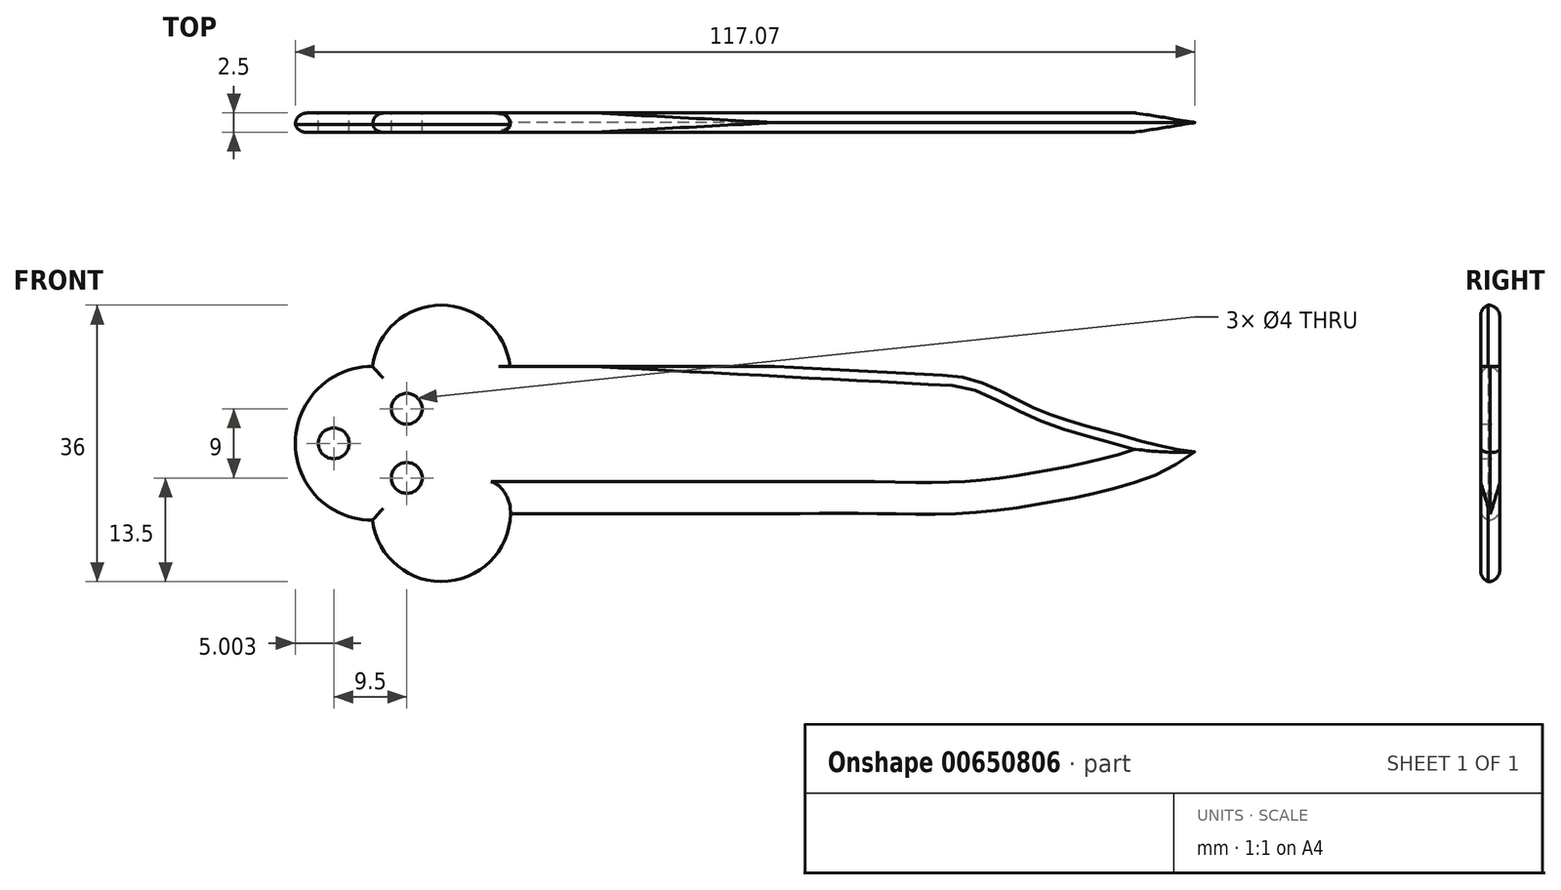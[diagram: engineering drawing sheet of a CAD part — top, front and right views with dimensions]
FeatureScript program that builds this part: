
annotation { "Feature Type Name" : "Feature", "Feature Type Description" : "" }
export const myFeature = defineFeature(function(context is Context, id is Id, definition is map)
    precondition{}
    {
        {
            var Q0;
            Q0=qCreatedBy(makeId("Front.planeOp"),FACE);
            var sketch = newSketch(context, id + "F0", { "sketchPlane" : qUnion([Q0])});
            skLineSegment(sketch, "E0", {"start": v(-50.99, 0) * mm, "end": v(69.01, 0) * mm});
            skPoint(sketch, "E1", {"position": v(-40.99, 0) * mm});
            skPoint(sketch, "E2", {"position": v(-31.99, 0) * mm});
            skCircle(sketch, "E3", {"center": v(-40.99, 0) * mm, "radius": 10 * mm});
            skLineSegment(sketch, "E4", {"start": v(-31.99, 9) * mm, "end": v(-31.99, 0) * mm});
            skLineSegment(sketch, "E5", {"start": v(-31.99, -9) * mm, "end": v(-31.99, 0) * mm});
            skCircle(sketch, "E6", {"center": v(-31.99, 9) * mm, "radius": 9 * mm});
            skCircle(sketch, "E7", {"center": v(-31.99, -9) * mm, "radius": 9 * mm});
            skLineSegment(sketch, "E8", {"start": v(-40.99, 0) * mm, "end": v(-31.99, 9) * mm});
            skLineSegment(sketch, "E9", {"start": v(-40.99, 0) * mm, "end": v(-31.99, -9) * mm});
            skPoint(sketch, "E10", {"position": v(-36.49, 4.5) * mm});
            skPoint(sketch, "E11", {"position": v(-36.49, -4.5) * mm});
            skLineSegment(sketch, "E12", {"start": v(-50.99, 0) * mm, "end": v(-40.99, 0) * mm});
            skLineSegment(sketch, "E13", {"start": v(-50.99, 0) * mm, "end": v(-45.99, 0) * mm});
            skPoint(sketch, "E14", {"position": v(-45.99, 0) * mm});
            skCircle(sketch, "E15", {"center": v(-45.99, 0) * mm, "radius": 2 * mm});
            skCircle(sketch, "E16", {"center": v(-36.49, 4.5) * mm, "radius": 2 * mm});
            skCircle(sketch, "E17", {"center": v(-36.49, -4.5) * mm, "radius": 2 * mm});
            skPoint(sketch, "E18", {"position": v(-40.93, -10) * mm});
            skLineSegment(sketch, "E19", {"start": v(-40.93, -10) * mm, "end": v(-23.04, -10) * mm});
            skPoint(sketch, "E20", {"position": v(-40.93, 10) * mm});
            skLineSegment(sketch, "E21", {"start": v(-40.93, 10) * mm, "end": v(-23.04, 10) * mm});
            skLineSegment(sketch, "E22", {"start": v(-23.04, 10) * mm, "end": v(-23.04, -10) * mm});
            skLineSegment(sketch, "E23", {"start": v(-23.04, 10) * mm, "end": v(34.9, 10) * mm});
            skFitSpline(sketch, "E24", {"points": [v(34.9, 10) * mm, v(45.52, 5.83) * mm, v(55.56, 2.58) * mm, v(69.01, 0) * mm], "startDerivative": vector(32.43, -1.73) * mm, "endDerivative": vector(41.87, 0) * mm});
            skLineSegment(sketch, "E25", {"start": v(-23.04, -10) * mm, "end": v(7.16, -10) * mm});
            skFitSpline(sketch, "E26", {"points": [v(7.16, -10) * mm, v(14.98, -10) * mm, v(24.87, -10) * mm, v(35.5, -10) * mm, v(46.7, -8.63) * mm, v(61.16, -4.94) * mm, v(69.01, 0) * mm], "startDerivative": vector(52.92, -0.1) * mm, "endDerivative": vector(44.23, 34.13) * mm});
            skSolve(sketch);
        }
        {
            var Q0;
            Q0 = qSketchRegion(id + "F0", true);
            var Q1;
            {var subQ0=sQuery(id+"F0.wireOp",EDGE,"E23");Q1=makeQuery(id+"F0.imprint","IMPRINT",FACE,{"disambiguationData":[TD([[makeQuery(id+"F0.imprint","IMPRINT",EDGE,{"derivedFrom":subQ0}),-1.0]])]});}
            var Q2;
            {var subQ0=sQuery(id+"F0.wireOp",EDGE,"E4");var subQ1=sQuery(id+"F0.wireOp",EDGE,"E3");var subQ2=makeQuery(id+"F0.imprint","INTERSECT",VERTEX,{"derivedFrom":[subQ1,subQ0]});Q2=makeQuery(id+"F0.imprint","IMPRINT",FACE,{"disambiguationData":[TD([[makeQuery(id+"F0.imprint","IMPRINT",EDGE,{"disambiguationData":[TD([[subQ2,-1.0]])],"derivedFrom":subQ1}),-1.0]])]});}
            var Q3;
            {var subQ0=sQuery(id+"F0.wireOp",EDGE,"E3");var subQ1=sQuery(id+"F0.wireOp",EDGE,"E0");var subQ2=makeQuery(id+"F0.imprint","INTERSECT",VERTEX,{"derivedFrom":[subQ1,subQ0]});Q3=makeQuery(id+"F0.imprint","IMPRINT",FACE,{"disambiguationData":[TD([[makeQuery(id+"F0.imprint","IMPRINT",EDGE,{"disambiguationData":[TD([[subQ2,-1.0]])],"derivedFrom":subQ1}),1.0]])]});}
            var Q4;
            {var subQ0=sQuery(id+"F0.wireOp",EDGE,"E3");var subQ1=sQuery(id+"F0.wireOp",EDGE,"E0");var subQ2=makeQuery(id+"F0.imprint","INTERSECT",VERTEX,{"derivedFrom":[subQ1,subQ0]});Q4=makeQuery(id+"F0.imprint","IMPRINT",FACE,{"disambiguationData":[TD([[makeQuery(id+"F0.imprint","IMPRINT",EDGE,{"disambiguationData":[TD([[subQ2,-1.0]])],"derivedFrom":subQ1}),-1.0]])]});}
            var Q5;
            {var subQ0=sQuery(id+"F0.wireOp",EDGE,"E9");var subQ3=sQuery(id+"F0.wireOp",EDGE,"E7");var subQ5=makeQuery(id+"F0.imprint","INTERSECT",VERTEX,{"derivedFrom":[subQ3,subQ0]});Q5=makeQuery(id+"F0.imprint","IMPRINT",FACE,{"disambiguationData":[TD([[makeQuery(id+"F0.imprint","IMPRINT",EDGE,{"disambiguationData":[TD([[subQ5,1.0]])],"derivedFrom":subQ0}),1.0]])]});}
            var Q6;
            {var subQ0=sQuery(id+"F0.wireOp",EDGE,"E9");var subQ1=sQuery(id+"F0.wireOp",EDGE,"E3");var subQ2=makeQuery(id+"F0.imprint","INTERSECT",VERTEX,{"derivedFrom":[subQ1,subQ0]});Q6=makeQuery(id+"F0.imprint","IMPRINT",FACE,{"disambiguationData":[TD([[makeQuery(id+"F0.imprint","IMPRINT",EDGE,{"disambiguationData":[TD([[subQ2,-1.0]])],"derivedFrom":subQ1}),-1.0]])]});}
            var Q7;
            {var subQ0=sQuery(id+"F0.wireOp",EDGE,"E5");var subQ1=sQuery(id+"F0.wireOp",EDGE,"E3");var subQ2=makeQuery(id+"F0.imprint","INTERSECT",VERTEX,{"derivedFrom":[subQ1,subQ0]});Q7=makeQuery(id+"F0.imprint","IMPRINT",FACE,{"disambiguationData":[TD([[makeQuery(id+"F0.imprint","IMPRINT",EDGE,{"disambiguationData":[TD([[subQ2,-1.0]])],"derivedFrom":subQ1}),1.0]])]});}
            var Q8;
            {var subQ0=sQuery(id+"F0.wireOp",EDGE,"E6");var subQ1=sQuery(id+"F0.wireOp",EDGE,"E3");var subQ2=makeQuery(id+"F0.imprint","INTERSECT",VERTEX,{"derivedFrom":[subQ1,subQ0]});Q8=makeQuery(id+"F0.imprint","IMPRINT",FACE,{"disambiguationData":[TD([[makeQuery(id+"F0.imprint","IMPRINT",EDGE,{"disambiguationData":[TD([[subQ2,-1.0]])],"derivedFrom":subQ1}),1.0]])]});}
            var Q9;
            {var subQ0=sQuery(id+"F0.wireOp",EDGE,"E8");var subQ3=sQuery(id+"F0.wireOp",EDGE,"E6");var subQ5=makeQuery(id+"F0.imprint","INTERSECT",VERTEX,{"derivedFrom":[subQ3,subQ0]});Q9=makeQuery(id+"F0.imprint","IMPRINT",FACE,{"disambiguationData":[TD([[makeQuery(id+"F0.imprint","IMPRINT",EDGE,{"disambiguationData":[TD([[subQ5,1.0]])],"derivedFrom":subQ0}),-1.0]])]});}
            var Q10;
            {var subQ3=sQuery(id+"F0.wireOp",EDGE,"E3");var subQ5=sQuery(id+"F0.wireOp",EDGE,"E9");var subQ9=makeQuery(id+"F0.imprint","INTERSECT",VERTEX,{"derivedFrom":[subQ3,subQ5]});Q10=makeQuery(id+"F0.imprint","IMPRINT",FACE,{"disambiguationData":[TD([[makeQuery(id+"F0.imprint","IMPRINT",EDGE,{"disambiguationData":[TD([[subQ9,-1.0]])],"derivedFrom":subQ3}),1.0]])]});}
            var Q11;
            {var subQ1=sQuery(id+"F0.wireOp",EDGE,"E4");var subQ7=sQuery(id+"F0.wireOp",EDGE,"E3");var subQ8=makeQuery(id+"F0.imprint","INTERSECT",VERTEX,{"derivedFrom":[subQ7,subQ1]});Q11=makeQuery(id+"F0.imprint","IMPRINT",FACE,{"disambiguationData":[TD([[makeQuery(id+"F0.imprint","IMPRINT",EDGE,{"disambiguationData":[TD([[subQ8,-1.0]])],"derivedFrom":subQ7}),1.0]])]});}
            var Q12;
            {var subQ1=sQuery(id+"F0.wireOp",EDGE,"E0");var subQ3=sQuery(id+"F0.wireOp",EDGE,"E3");var subQ4=makeQuery(id+"F0.imprint","INTERSECT",VERTEX,{"derivedFrom":[subQ1,subQ3]});Q12=makeQuery(id+"F0.imprint","IMPRINT",FACE,{"disambiguationData":[TD([[makeQuery(id+"F0.imprint","IMPRINT",EDGE,{"disambiguationData":[TD([[subQ4,-1.0]])],"derivedFrom":subQ3}),1.0]])]});}
            var Q13;
            {var subQ1=sQuery(id+"F0.wireOp",EDGE,"E0");var subQ3=sQuery(id+"F0.wireOp",EDGE,"E3");var subQ4=makeQuery(id+"F0.imprint","INTERSECT",VERTEX,{"derivedFrom":[subQ1,subQ3]});Q13=makeQuery(id+"F0.imprint","IMPRINT",FACE,{"disambiguationData":[TD([[makeQuery(id+"F0.imprint","IMPRINT",EDGE,{"disambiguationData":[TD([[subQ4,1.0]])],"derivedFrom":subQ3}),1.0]])]});}
            extrude(context, id + "F1", {"entities" : qUnion([Q0, Q1, Q2, Q3, Q4, Q5, Q6, Q7, Q8, Q9, Q10, Q11, Q12, Q13]), "endBound" : BoundingType.SYMMETRIC, "depth" : 2.5 * mm, "offsetDistance" : 25 * mm});
        }
        {
            var Q0;
            {var subQ0=sQuery(id+"F0.wireOp",EDGE,"E21");var subQ1=sQuery(id+"F0.wireOp",EDGE,"E6");Q0=makeQuery(id+"F1.opExtrude","CAP_EDGE",EDGE,{"disambiguationData":[OSD([subQ1]),TDD([makeQuery(id+"F0.imprint","IMPRINT",EDGE,{"disambiguationData":[TD([[makeQuery(id+"F0.imprint","INTERSECT",VERTEX,{"derivedFrom":[sQuery(id+"F0.wireOp",EDGE,"E3"),subQ1,subQ0]}),1.0]])],"derivedFrom":subQ1})])],"isStart":true});}
            var Q1;
            {var subQ0=sQuery(id+"F0.wireOp",EDGE,"E3");var subQ1=makeQuery(id+"F0.imprint","INTERSECT",VERTEX,{"derivedFrom":[subQ0,sQuery(id+"F0.wireOp",EDGE,"E13")]});Q1=makeQuery(id+"F1.opExtrude","CAP_EDGE",EDGE,{"disambiguationData":[OSD([subQ0]),TDD([makeQuery(id+"F0.imprint","IMPRINT",EDGE,{"disambiguationData":[TD([[subQ1,1.0]])],"derivedFrom":subQ0}),makeQuery(id+"F0.imprint","IMPRINT",EDGE,{"disambiguationData":[TD([[subQ1,-1.0]])],"derivedFrom":subQ0})])],"isStart":true});}
            var Q2;
            {var subQ0=sQuery(id+"F0.wireOp",EDGE,"E19");var subQ1=sQuery(id+"F0.wireOp",EDGE,"E7");Q2=makeQuery(id+"F1.opExtrude","CAP_EDGE",EDGE,{"disambiguationData":[OSD([subQ1]),TDD([makeQuery(id+"F0.imprint","IMPRINT",EDGE,{"disambiguationData":[TD([[makeQuery(id+"F0.imprint","INTERSECT",VERTEX,{"derivedFrom":[sQuery(id+"F0.wireOp",EDGE,"E3"),subQ1,subQ0]}),-1.0]])],"derivedFrom":subQ1})])],"isStart":true});}
            fillet(context, id + "F2", {"entities" : qUnion([Q0, Q1, Q2]), "radius" : 1.5 * mm, "tangentPropagation" : true, "defaultsChanged" : false, "vertexSettings" : [], "allowEdgeOverflow" : false});
        }
        {
            var Q0;
            {var subQ0=sQuery(id+"F0.wireOp",EDGE,"E19");var subQ1=sQuery(id+"F0.wireOp",EDGE,"E7");Q0=makeQuery(id+"F1.opExtrude","CAP_EDGE",EDGE,{"disambiguationData":[OSD([subQ1]),TDD([makeQuery(id+"F0.imprint","IMPRINT",EDGE,{"disambiguationData":[TD([[makeQuery(id+"F0.imprint","INTERSECT",VERTEX,{"derivedFrom":[sQuery(id+"F0.wireOp",EDGE,"E3"),subQ1,subQ0]}),-1.0]])],"derivedFrom":subQ1})])],"isStart":false});}
            var Q1;
            {var subQ0=sQuery(id+"F0.wireOp",EDGE,"E3");var subQ1=makeQuery(id+"F0.imprint","INTERSECT",VERTEX,{"derivedFrom":[subQ0,sQuery(id+"F0.wireOp",EDGE,"E13")]});Q1=makeQuery(id+"F1.opExtrude","CAP_EDGE",EDGE,{"disambiguationData":[OSD([subQ0]),TDD([makeQuery(id+"F0.imprint","IMPRINT",EDGE,{"disambiguationData":[TD([[subQ1,1.0]])],"derivedFrom":subQ0}),makeQuery(id+"F0.imprint","IMPRINT",EDGE,{"disambiguationData":[TD([[subQ1,-1.0]])],"derivedFrom":subQ0})])],"isStart":false});}
            var Q2;
            {var subQ0=sQuery(id+"F0.wireOp",EDGE,"E21");var subQ1=sQuery(id+"F0.wireOp",EDGE,"E6");Q2=makeQuery(id+"F1.opExtrude","CAP_EDGE",EDGE,{"disambiguationData":[OSD([subQ1]),TDD([makeQuery(id+"F0.imprint","IMPRINT",EDGE,{"disambiguationData":[TD([[makeQuery(id+"F0.imprint","INTERSECT",VERTEX,{"derivedFrom":[sQuery(id+"F0.wireOp",EDGE,"E3"),subQ1,subQ0]}),1.0]])],"derivedFrom":subQ1})])],"isStart":false});}
            fillet(context, id + "F3", {"entities" : qUnion([Q0, Q1, Q2]), "radius" : 1.5 * mm, "tangentPropagation" : true, "defaultsChanged" : false, "vertexSettings" : [], "allowEdgeOverflow" : false});
        }
        {
            var Q0;
            Q0=makeQuery(id+"F1.opExtrude","CAP_EDGE",EDGE,{"disambiguationData":[OSD([sQuery(id+"F0.wireOp",EDGE,"E25")])],"isStart":false});
            var Q1;
            Q1=makeQuery(id+"F1.opExtrude","CAP_EDGE",EDGE,{"disambiguationData":[OSD([sQuery(id+"F0.wireOp",EDGE,"E26")])],"isStart":false});
            chamfer(context, id + "F4", {"entities" : qUnion([Q0, Q1]), "chamferType" : ChamferType.OFFSET_ANGLE, "width" : 5 * mm, "oppositeDirection" : false, "angle" : 17 * degree, "tangentPropagation" : true});
        }
        {
            var Q0;
            Q0=makeQuery(id+"F1.opExtrude","CAP_EDGE",EDGE,{"disambiguationData":[OSD([sQuery(id+"F0.wireOp",EDGE,"E25")])],"isStart":true});
            var Q1;
            Q1=makeQuery(id+"F1.opExtrude","CAP_EDGE",EDGE,{"disambiguationData":[OSD([sQuery(id+"F0.wireOp",EDGE,"E26")])],"isStart":true});
            chamfer(context, id + "F5", {"entities" : qUnion([Q0, Q1]), "chamferType" : ChamferType.OFFSET_ANGLE, "width" : 4.9 * mm, "oppositeDirection" : true, "angle" : 17 * degree, "tangentPropagation" : true});
        }
        {
            var Q0;
            Q0=makeQuery(id+"F1.opExtrude","CAP_EDGE",EDGE,{"disambiguationData":[OSD([sQuery(id+"F0.wireOp",EDGE,"E24")])],"isStart":true});
            var Q1;
            Q1=makeQuery(id+"F1.opExtrude","CAP_EDGE",EDGE,{"disambiguationData":[OSD([sQuery(id+"F0.wireOp",EDGE,"E24")])],"isStart":false});
            chamfer(context, id + "F6", {"entities" : qUnion([Q0, Q1]), "chamferType" : ChamferType.OFFSET_ANGLE, "width" : 2.5 * mm, "oppositeDirection" : true, "angle" : 45 * degree, "tangentPropagation" : true});
        }
    });
